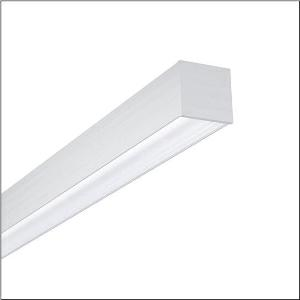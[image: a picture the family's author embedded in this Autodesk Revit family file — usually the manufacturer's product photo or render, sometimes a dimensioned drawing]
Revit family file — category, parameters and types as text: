
# Revit family: silica_r_5mx21bd2e4a_11e7
name_source: partatom
category: Lighting Fixtures
units: mm (PartAtom-declared; Revit-internal decimal feet)

## family parameters
Cut with Voids When Loaded = No
Host = Face
Light Source = No
Part Type = Normal
Room Calculation Point = No
Round Connector Dimension = Use Diameter
Shared = No

## types (1)
- --- (1 x LED, 9910 lm, 60.1 W, 4000K)
    Apparent Load = 60 VA
    CIE Flux Codes = 82 97 100 100 100
    Color Rendering = 80
    Color Temperature = 4000K
    Default Elevation = 1800 mm
    Description = Silica®, office luminaire, of aluminium, light emission: direct distribution, primary light characteristic: symmetric, installation type: surface-mounted, LED, rated luminous flux: 9.910lm, luminous efficacy: 165lm/W, light colour: 840, colour temperature: 4000K, control gear: ECG DALI, with terminal, 3+2-pole, max. 2.5mm², mains connection: 230V, AC, 50/60Hz, rated input power: 60W, luminaire housing, of aluminium, anodised, silver, length: 2.844mm, width: 65mm, height: 64mm, protection rating (complete): IP20, insulation class (complete): insulation class I (protective earthing), certification: CE, permissible operating ambient temperature: 0..+35°C, standard: EN 50419, packaging unit: 1 piece
    Height = 64 mm
    Lamp = 1 x LED
    Lamp Light Flux = 9910 lm
    Lamp Power = 60.1 W
    Lamp count = 1
    Length = 2845 mm
    Luminous efficacy = 165 lm/W
    Manufacturer = Siteco
    ModVariant = No
    Model = 5MX21BD2E4A
    Mounting Place = Ceiling
    Mounting Type = Surface mounted
    Number of Poles = 1
    OnlyDefault = Yes
    Power Factor = 1
    Product Name = Silica®
    Product group = office luminaire | ceiling mounted
    ProductGroupID = 304
    Protection Class = Protection class I
    Protection Degree = IP 20
    RLX_Detail_Level = 1
    RLX_Emergency_Light_Flux = 0 lm
    RLX_Emergency_Type = 0
    RLX_Emergency_Type_DB = No
    RlxData = <blob elided: 27197 chars, md5=2dc67d4b>
    Socket = socket
    Standby Power = 0 W
    System Light Flux = 9910 lm
    System Power = 60 W
    Type Comments = factory setting: luminous flux: 100 % | dim-lin: 254 | 336 mA
    Type Image = l_1004827.jpg
    URL = http://relux.com
    VarID = @adj_138638
    Voltage = 0 V
    Weight = 0.00 kg
    Width = 66 mm

## geometry (parser evidence)
native form markers: Blend x4, Sweep x11
no freeform markers — native parametric forms only
